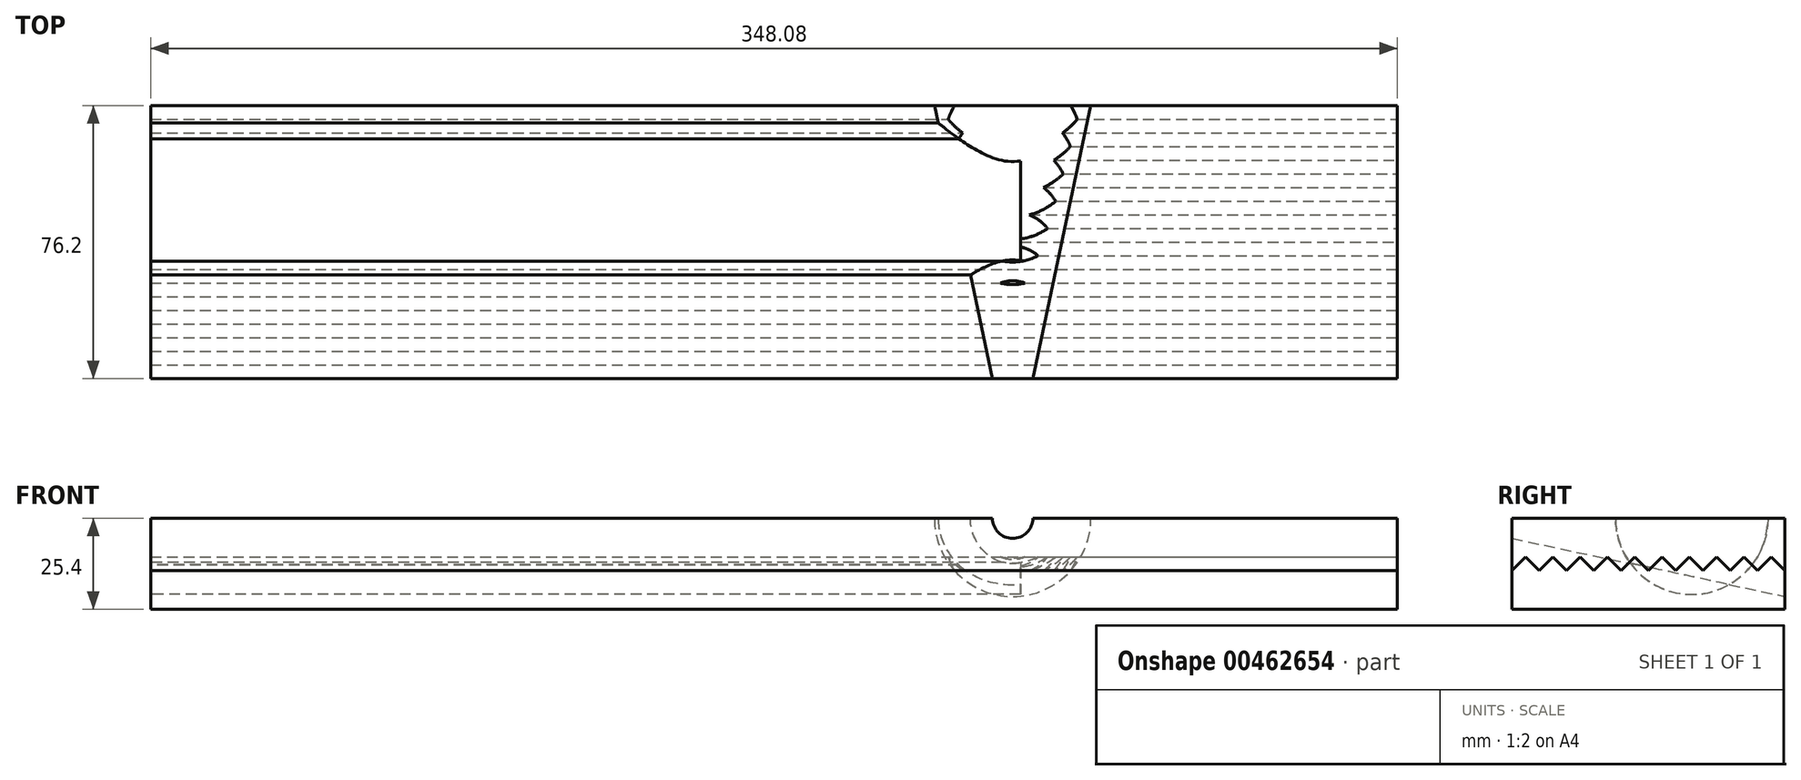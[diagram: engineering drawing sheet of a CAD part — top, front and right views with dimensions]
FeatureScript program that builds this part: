
annotation { "Feature Type Name" : "Feature", "Feature Type Description" : "" }
export const myFeature = defineFeature(function(context is Context, id is Id, definition is map)
    precondition{}
    {
        {
            var Q0;
            Q0=qCreatedBy(makeId("Top.planeOp"),FACE);
            var sketch = newSketch(context, id + "F0", { "sketchPlane" : qUnion([Q0])});
            skLineSegment(sketch, "E0.bottom", {"start": v(0, 0) * mm, "end": v(348.08, 0) * mm});
            skLineSegment(sketch, "E0.top", {"start": v(0, 76.2) * mm, "end": v(348.08, 76.2) * mm});
            skLineSegment(sketch, "E0.left", {"start": v(0, 0) * mm, "end": v(0, 76.2) * mm});
            skLineSegment(sketch, "E0.right", {"start": v(348.08, 0) * mm, "end": v(348.08, 76.2) * mm});
            skSolve(sketch);
        }
        {
            var Q0;
            Q0 = qSketchRegion(id + "F0", true);
            var Q1;
            Q1 = qSketchRegion(id + "F2", true);
            extrude(context, id + "F1", {"entities" : qUnion([Q0, Q1]), "depth" : 25.4 * mm});
        }
        {
            var Q0;
            Q0=makeQuery(id+"F1.opExtrude","SWEPT_FACE",FACE,{"disambiguationData":[OSD([sQuery(id+"F0.wireOp",EDGE,"E0.right")])]});
            var sketch = newSketch(context, id + "F2", { "sketchPlane" : qUnion([Q0])});
            skLineSegment(sketch, "E1", {"start": v(0, 10.8) * mm, "end": v(3.81, 14.6) * mm});
            skLineSegment(sketch, "E2", {"start": v(3.81, 14.6) * mm, "end": v(7.62, 10.8) * mm});
            skLineSegment(sketch, "E3", {"start": v(76.2, 12.7) * mm, "end": v(0, 12.7) * mm, "construction": true});
            skLineSegment(sketch, "E4.1.0.0", {"start": v(7.62, 10.8) * mm, "end": v(11.43, 14.6) * mm});
            skLineSegment(sketch, "E4.1.0.1", {"start": v(11.43, 14.6) * mm, "end": v(15.24, 10.8) * mm});
            skLineSegment(sketch, "E4.2.0.0", {"start": v(15.24, 10.8) * mm, "end": v(19.05, 14.6) * mm});
            skLineSegment(sketch, "E4.2.0.1", {"start": v(19.05, 14.6) * mm, "end": v(22.86, 10.8) * mm});
            skLineSegment(sketch, "E4.3.0.0", {"start": v(22.86, 10.8) * mm, "end": v(26.67, 14.6) * mm});
            skLineSegment(sketch, "E4.3.0.1", {"start": v(26.67, 14.6) * mm, "end": v(30.48, 10.8) * mm});
            skLineSegment(sketch, "E4.4.0.0", {"start": v(30.48, 10.8) * mm, "end": v(34.3, 14.6) * mm});
            skLineSegment(sketch, "E4.4.0.1", {"start": v(34.3, 14.6) * mm, "end": v(38.1, 10.8) * mm});
            skLineSegment(sketch, "E4.5.0.0", {"start": v(38.1, 10.8) * mm, "end": v(41.91, 14.6) * mm});
            skLineSegment(sketch, "E4.5.0.1", {"start": v(41.91, 14.6) * mm, "end": v(45.72, 10.8) * mm});
            skLineSegment(sketch, "E4.6.0.0", {"start": v(45.72, 10.8) * mm, "end": v(49.53, 14.6) * mm});
            skLineSegment(sketch, "E4.6.0.1", {"start": v(49.53, 14.6) * mm, "end": v(53.34, 10.8) * mm});
            skLineSegment(sketch, "E4.7.0.0", {"start": v(53.34, 10.8) * mm, "end": v(57.15, 14.6) * mm});
            skLineSegment(sketch, "E4.7.0.1", {"start": v(57.15, 14.6) * mm, "end": v(60.96, 10.8) * mm});
            skLineSegment(sketch, "E4.direction1", {"start": v(0, 10.8) * mm, "end": v(7.62, 10.8) * mm, "construction": true});
            skLineSegment(sketch, "E5.0.8.0", {"start": v(60.96, 10.8) * mm, "end": v(64.77, 14.6) * mm});
            skLineSegment(sketch, "E5.3.8.0", {"start": v(64.77, 14.6) * mm, "end": v(68.58, 10.8) * mm});
            skLineSegment(sketch, "E5.0.9.0", {"start": v(68.58, 10.8) * mm, "end": v(72.4, 14.6) * mm});
            skLineSegment(sketch, "E5.3.9.0", {"start": v(72.39, 14.6) * mm, "end": v(76.2, 10.8) * mm});
            skLineSegment(sketch, "E6.1.0.0", {"start": v(22.86, 10.77) * mm, "end": v(26.67, 14.58) * mm});
            skLineSegment(sketch, "E6.1.0.1", {"start": v(34.3, 14.58) * mm, "end": v(38.1, 10.77) * mm});
            skLineSegment(sketch, "E6.1.0.2", {"start": v(19.05, 14.58) * mm, "end": v(22.86, 10.77) * mm});
            skLineSegment(sketch, "E6.1.0.3", {"start": v(57.15, 14.58) * mm, "end": v(60.96, 10.77) * mm});
            skLineSegment(sketch, "E6.1.0.4", {"start": v(30.48, 10.77) * mm, "end": v(34.3, 14.58) * mm});
            skLineSegment(sketch, "E6.1.0.5", {"start": v(76.2, 12.67) * mm, "end": v(0, 12.67) * mm, "construction": true});
            skLineSegment(sketch, "E6.1.0.6", {"start": v(38.1, 10.77) * mm, "end": v(41.91, 14.58) * mm});
            skLineSegment(sketch, "E6.1.0.7", {"start": v(53.34, 10.77) * mm, "end": v(57.15, 14.58) * mm});
            skLineSegment(sketch, "E6.1.0.8", {"start": v(0, 10.77) * mm, "end": v(3.81, 14.58) * mm});
            skLineSegment(sketch, "E6.1.0.9", {"start": v(26.67, 14.58) * mm, "end": v(30.48, 10.77) * mm});
            skLineSegment(sketch, "E6.1.0.10", {"start": v(11.43, 14.58) * mm, "end": v(15.24, 10.77) * mm});
            skLineSegment(sketch, "E6.1.0.11", {"start": v(49.53, 14.58) * mm, "end": v(53.34, 10.77) * mm});
            skLineSegment(sketch, "E6.1.0.12", {"start": v(41.91, 14.58) * mm, "end": v(45.72, 10.77) * mm});
            skLineSegment(sketch, "E6.1.0.13", {"start": v(3.81, 14.58) * mm, "end": v(7.62, 10.77) * mm});
            skLineSegment(sketch, "E6.1.0.14", {"start": v(0, 10.77) * mm, "end": v(7.62, 10.77) * mm, "construction": true});
            skLineSegment(sketch, "E6.1.0.15", {"start": v(68.58, 10.77) * mm, "end": v(72.4, 14.58) * mm});
            skLineSegment(sketch, "E6.1.0.16", {"start": v(15.24, 10.77) * mm, "end": v(19.05, 14.58) * mm});
            skLineSegment(sketch, "E6.1.0.17", {"start": v(60.96, 10.77) * mm, "end": v(64.77, 14.58) * mm});
            skLineSegment(sketch, "E6.1.0.18", {"start": v(45.72, 10.77) * mm, "end": v(49.53, 14.58) * mm});
            skLineSegment(sketch, "E6.1.0.19", {"start": v(72.4, 14.58) * mm, "end": v(76.2, 10.77) * mm});
            skLineSegment(sketch, "E6.1.0.20", {"start": v(64.77, 14.58) * mm, "end": v(68.58, 10.77) * mm});
            skLineSegment(sketch, "E6.1.0.21", {"start": v(7.62, 10.77) * mm, "end": v(11.43, 14.58) * mm});
            skLineSegment(sketch, "E6.direction1", {"start": v(0, 10.8) * mm, "end": v(0, 10.77) * mm, "construction": true});
            skLineSegment(sketch, "E7", {"start": v(0, 10.8) * mm, "end": v(0, 10.77) * mm});
            skLineSegment(sketch, "E8", {"start": v(76.2, 10.8) * mm, "end": v(76.2, 10.77) * mm});
            skSolve(sketch);
        }
        {
            var Q0;
            Q0 = qSketchRegion(id + "F2", true);
            extrude(context, id + "F3", {"entities" : qUnion([Q0]), "operationType" : NewBodyOperationType.REMOVE, "endBound" : BoundingType.THROUGH_ALL, "oppositeDirection" : true, "depth" : 25.4 * mm});
        }
        {
            var Q0;
            {var subQ2=sQuery(id+"F0.wireOp",EDGE,"E0.top");Q0=makeQuery(id+"F3.boolean.opBoolean","SPLIT",FACE,{"disambiguationData":[TD([makeQuery(id+"F3.opExtrude","SWEPT_FACE",FACE,{"disambiguationData":[OSD([sQuery(id+"F2.wireOp",EDGE,"E5.3.9.0")])]})])],"derivedFrom":makeQuery(id+"F1.opExtrude","SWEPT_FACE",FACE,{"disambiguationData":[OSD([subQ2])]})});}
            var sketch = newSketch(context, id + "F4", { "sketchPlane" : qUnion([Q0])});
            skCircle(sketch, "E9", {"center": v(-240.65, 25.4) * mm, "radius": 21.83 * mm});
            skSolve(sketch);
        }
        {
            var Q0;
            Q0 = qSketchRegion(id + "F4", true);
            extrude(context, id + "F5", {"entities" : qUnion([Q0]), "operationType" : NewBodyOperationType.REMOVE, "oppositeDirection" : true, "depth" : 76.96 * mm, "hasDraft" : true, "draftAngle" : 12 * degree, "draftPullDirection" : true});
        }
        {
            var Q0;
            {var subQ1=sQuery(id+"F0.wireOp",EDGE,"E0.left");Q0=makeQuery(id+"F3.boolean.opBoolean","SPLIT",FACE,{"disambiguationData":[TD([makeQuery(id+"F3.opExtrude","SWEPT_FACE",FACE,{"disambiguationData":[OSD([sQuery(id+"F2.wireOp",EDGE,"E1")])]})])],"derivedFrom":makeQuery(id+"F1.opExtrude","SWEPT_FACE",FACE,{"disambiguationData":[OSD([subQ1])]})});}
            var sketch = newSketch(context, id + "F6", { "sketchPlane" : qUnion([Q0])});
            skCircle(sketch, "E10", {"center": v(-50.16, 25.4) * mm, "radius": 21.25 * mm});
            skSolve(sketch);
        }
        {
            var Q0;
            Q0 = qSketchRegion(id + "F6", true);
            extrude(context, id + "F7", {"entities" : qUnion([Q0]), "operationType" : NewBodyOperationType.REMOVE, "oppositeDirection" : true, "depth" : 242.82 * mm});
        }
    });
